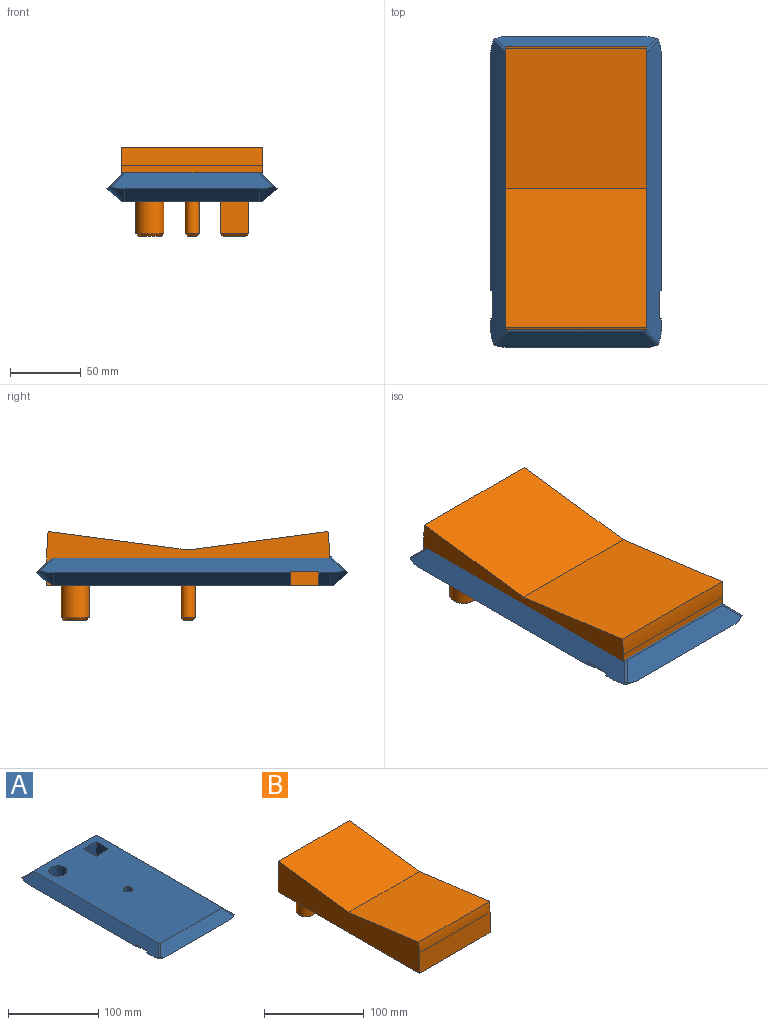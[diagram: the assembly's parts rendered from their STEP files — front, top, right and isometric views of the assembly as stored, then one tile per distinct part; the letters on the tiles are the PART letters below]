
ASSEMBLY  parts=2 mates=1
PART A: 30 faces, bbox 124.8x224.8x20.2 mm
  f0: plane 118x20mm, normal (0,0,-1), area 2360mm2, adj f17,f18,f28,f29
  f1: plane 10.33x8.67mm, normal (-0.64,0,-0.77), area 107.9mm2, adj f3,f18,f25,f28
  f2: plane 168x10.33mm, normal (0.64,0,-0.77), area 2265.7mm2, adj f4,f17,f21,f29
  f3: plane 100x10mm, normal (0,0,-1), area 998.3mm2, adj f1,f6,f7,f25,f27,f28
  f4: plane 170x100mm, normal (0,0,-1), area 16205.6mm2, adj f2,f5,f8,f9,f10,f11,f12,f13
  f5: plane 168x10.33mm, normal (-0.64,0,-0.77), area 2265.7mm2, adj f4,f18,f23,f29
  f6: plane 96x10.33mm, normal (0,-0.64,-0.77), area 1294.7mm2, adj f3,f19,f25,f27
  f7: plane 10.33x8.67mm, normal (0.64,0,-0.77), area 107.9mm2, adj f3,f17,f27,f28
  f8: plane 96x10.33mm, normal (0,0.64,-0.77), area 1294.7mm2, adj f4,f16,f21,f23
  f9: plane 20x20mm, normal (1,0,0), area 400mm2, adj f4,f10,f12,f15
  f10: plane 20x20mm, normal (0,-1,0), area 400mm2, adj f4,f9,f11,f15
  f11: plane 20x20mm, normal (-1,0,0), area 400mm2, adj f4,f10,f12,f15
  f12: plane 20x20mm, normal (0,1,0), area 400mm2, adj f4,f9,f11,f15
  f13: cylinder r=5mm len=20mm, axis (0,0,-1), area 628.3mm2, adj f4,f15
  f14: cylinder r=10mm len=20mm, axis (0,0,-1), area 1256.6mm2, adj f4,f15
  f15: plane 198x98mm, normal (0,0,1), area 18609.8mm2, adj f9,f10,f11,f12,f13,f14,f16,f17
  f16: plane 114.67x11.33mm, normal (0,0.71,0.71), area 1689mm2, adj f8,f15,f20,f21,f22,f23
  f17: plane 214.67x11.33mm, normal (0.71,0,0.71), area 3253.9mm2, adj f0,f2,f7,f15,f20,f21,f26,f27
  f18: plane 214.67x11.33mm, normal (-0.71,0,0.71), area 3253.9mm2, adj f0,f1,f5,f15,f22,f23,f24,f25
  f19: plane 114.67x11.33mm, normal (0,-0.71,0.71), area 1689mm2, adj f6,f15,f24,f25,f26,f27
  f20: cylinder r=2mm len=11.16mm, axis (-0.58,-0.58,0.58), area 34.8mm2, adj f15,f16,f17,f21
  f21: cone r=2mm half-angle=50deg, axis (0,0,1), area 171.4mm2, adj f2,f4,f8,f16,f17,f20
  f22: cylinder r=2mm len=11.16mm, axis (0.58,-0.58,0.58), area 34.8mm2, adj f15,f16,f18,f23
  f23: cone r=2mm half-angle=50deg, axis (0,0,1), area 171.4mm2, adj f4,f5,f8,f16,f18,f22
  f24: cylinder r=2mm len=11.16mm, axis (-0.58,-0.58,-0.58), area 34.8mm2, adj f15,f18,f19,f25
  f25: cone r=2mm half-angle=50deg, axis (0,0,1), area 171.4mm2, adj f1,f3,f6,f18,f19,f24
  f26: cylinder r=2mm len=11.16mm, axis (0.58,-0.58,-0.58), area 34.8mm2, adj f15,f17,f19,f27
  f27: cone r=2mm half-angle=50deg, axis (0,0,1), area 171.4mm2, adj f3,f6,f7,f17,f19,f26
  f28: plane 120.66x10mm, normal (0,1,0), area 1115.3mm2, adj f0,f1,f3,f7,f17,f18
  f29: plane 120.66x10mm, normal (0,-1,0), area 1115.3mm2, adj f0,f2,f4,f5,f17,f18
PART B: 28 faces, bbox 100x200x63.1 mm
  f0: plane 200x100mm, normal (0,0,-1), area 19168mm2, adj f1,f2,f3,f4,f5,f7,f9,f10
  f1: plane 100x25mm, normal (0,-1,0), area 2500mm2, adj f0,f2,f4,f22
  f2: plane 200x38.05mm, normal (1,0,0), area 6309mm2, adj f0,f1,f3,f20,f21,f22,f23
  f3: plane 100x25mm, normal (0,1,0), area 2500mm2, adj f0,f2,f4,f20
  f4: plane 200x38.05mm, normal (-1,0,0), area 6309mm2, adj f0,f1,f3,f20,f21,f22,f23
  f5: cylinder r=5mm len=23mm, axis (0,0,1), area 722.6mm2, adj f0,f14
  f6: plane 6x6mm, normal (0,0,-1), area 28.3mm2, adj f14
  f7: cylinder r=10mm len=23mm, axis (0,0,1), area 1445.1mm2, adj f0,f15
  f8: plane 16x16mm, normal (0,0,-1), area 201.1mm2, adj f15
  f9: plane 23x20mm, normal (0,-1,0), area 460mm2, adj f0,f10,f12,f16
  f10: plane 23x20mm, normal (1,0,0), area 460mm2, adj f0,f9,f11,f17
  f11: plane 23x20mm, normal (0,1,0), area 460mm2, adj f0,f10,f12,f19
  f12: plane 23x20mm, normal (-1,0,0), area 460mm2, adj f0,f9,f11,f18
  f13: plane 16x16mm, normal (0,0,-1), area 256mm2, adj f16,f17,f18,f19
  f14: cone r=5mm half-angle=45deg, axis (0,0,1), area 71.1mm2, adj f5,f6
  f15: cone r=10mm half-angle=45deg, axis (0,0,1), area 159.9mm2, adj f7,f8
  f16: plane 20x2mm, normal (0,-0.71,-0.71), area 50.9mm2, adj f9,f13,f17,f18
  f17: plane 20x2mm, normal (0.71,0,-0.71), area 50.9mm2, adj f10,f13,f16,f19
  f18: plane 20x2mm, normal (-0.71,0,-0.71), area 50.9mm2, adj f12,f13,f16,f19
  f19: plane 20x2mm, normal (0,0.71,-0.71), area 50.9mm2, adj f11,f13,f17,f18
  f20: cylinder r=100mm len=100mm, axis (-1,0,0), area 1309mm2, adj f2,f3,f4,f21
  f21: plane 100x99.14mm, normal (0,-0.13,0.99), area 10000mm2, adj f2,f4,f20,f23
  f22: cylinder r=100mm len=100mm, axis (1,0,0), area 1309mm2, adj f1,f2,f4,f23
  f23: plane 100x99.14mm, normal (0,0.13,0.99), area 10000mm2, adj f2,f4,f21,f22
  f24: cylinder r=2.5mm len=10mm, axis (0,0,-1), area 157.1mm2, adj f0,f25
  f25: plane 5x5mm, normal (0,0,-1), area 19.6mm2, adj f24
  f26: cylinder r=2.5mm len=10mm, axis (0,0,-1), area 157.1mm2, adj f0,f27
  f27: plane 5x5mm, normal (0,0,-1), area 19.6mm2, adj f26
PLACE A rot(axis=(0.01,-1,-0.09),0deg) t=(-262.03,-46.26,-64.57)mm
PLACE B rot(axis=(0.01,-1,-0.09),0deg) t=(-157.73,56.54,-64.57)mm
MATE fastened B.f0 <-> A.f13  axis (0,0,-1) through (-312.03,53.74,-64.57)mm
